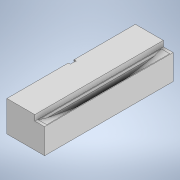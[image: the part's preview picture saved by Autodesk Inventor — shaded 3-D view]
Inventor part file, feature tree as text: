
AUTODESK INVENTOR PART (.ipt)
format: ipt  version: 2020 (Build 240168000, 168)  size: 215,040 bytes
history: native  units: mm
features: extrude x8, sketch x8, chamfer x6, direct_edit x1, draft x1, move_body x1
ambient origin geometry x8: Origin, YZ Plane, XZ Plane, XY Plane, X Axis, Y Axis, Z Axis, Center Point
bodies: Solid1 (feature_tree)
feature tree (25):
  extrude  "Extrusion1"  Depth=460.0mm
  extrude  "Extrusion2"  Depth=150.0mm
  extrude  "Extrusion3"  Depth=20.0mm
  chamfer  "Chamfer1"  Distance=62.0mm
  chamfer  "Chamfer2"  Distance=210.0mm
  chamfer  "Chamfer3"  Distance=210.0mm
  chamfer  "Chamfer4"  Distance=5.0mm
  direct_edit  "Direct Edit2"
  extrude  "Extrusion4"  TaperAngle=0.0deg  [1 undecoded]
  extrude  "Extrusion5"  Depth=20.0mm
  chamfer  "Chamfer5"  Distance=132.75mm
  chamfer  "Chamfer6"  Distance=20.0mm
  draft  "FaceDraft1"
  extrude  "Extrusion6"  Depth=20.0mm
  extrude  "Extrusion7"  Depth=20.0mm
  extrude  "Extrusion8"  Depth=20.0mm
  sketch  "Sketch1"  dims[d0=100.0mm d1=460.0mm]
  sketch  "Sketch2"  dims[d2=150.0mm d3=0.0mm d4=130.0mm]
  sketch  "Sketch3"  dims[d5=35.0mm d6=0.0mm d7=20.0mm]
  sketch  "Sketch4"  dims[d8=20.0mm d9=62.0mm d10=0.0mm d11=210.0mm d12=2.0mm d13=1.745329mm d14=210.0mm d15=2.0mm d16=1.745329mm d17=5.0mm d18=2.0mm d19=1.745329mm]
  sketch  "Sketch5"  dims[d20=5.0mm d21=2.0mm d22=1.745329mm d26=0.0mm d27=0.0mm d28=-40.0mm]
  sketch  "Sketch6"  dims[d29=20.0mm d30=20.0mm]
  sketch  "Sketch7"  dims[d31=30.0mm d32=132.75mm d33=0.0mm]
  sketch  "Sketch8"  dims[d34=230.0mm d35=20.0mm d36=0.0mm d37=20.0mm d38=2.0mm d39=1.745329mm d40=20.0mm d41=2.0mm d42=1.745329mm d43=0.872665mm d44=5.0mm d45=85.0mm d46=0.0mm d49=16.0mm d50=26.0mm d51=16.0mm d52=12.25mm d53=0.0mm d54=15.0mm d55=20.0mm d56=0.0mm d57=0.0mm]
  move_body  "Move2"
note: 1 required parameter value undecoded (feature->parameter linkage not recoverable at this tier; creation-order binding heuristic only, values carry confidence <= 0.55)
